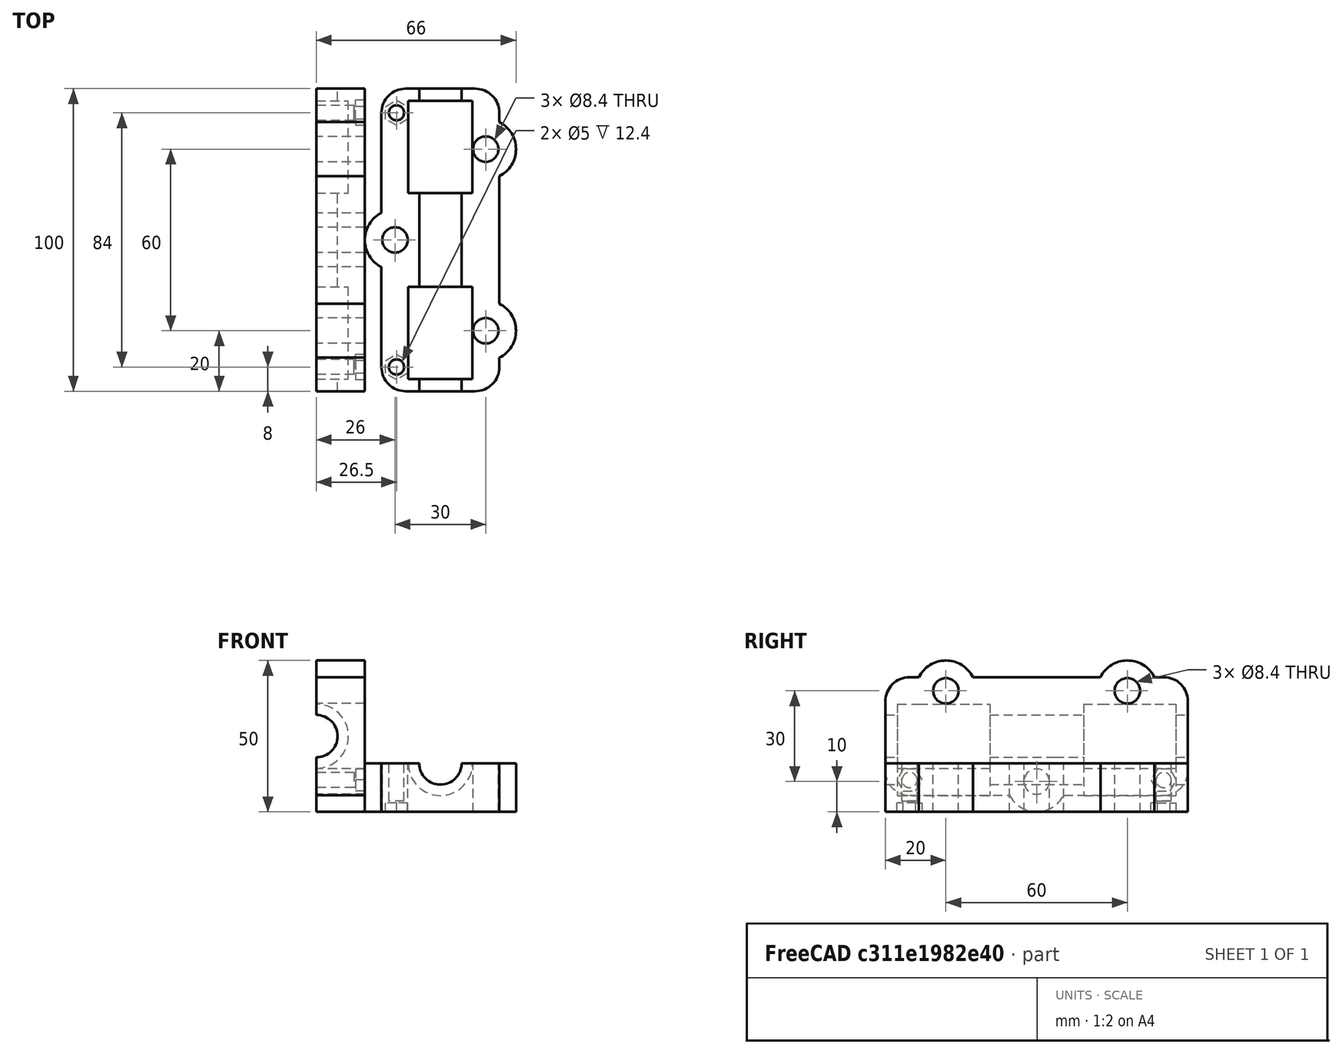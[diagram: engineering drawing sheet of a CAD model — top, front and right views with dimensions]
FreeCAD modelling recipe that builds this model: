
FCSTD DOCUMENT  (FreeCAD 0.15R4666 (Git))
Label: y_carriage_A
License: All rights reserved
LicenseURL: http://en.wikipedia.org/wiki/All_rights_reserved
objects: Part::Cylinder×11, Part::MultiFuse×5, Part::Cut×5, Part::Feature×2, Part::Prism×2, Mesh::Feature×1, Part::Box×1, Part::Fillet×1
note: 27 computed .brp shape members not serialized (recipe doc carries the construction recipe); baked Part::Feature solids carry a one-line shape summary decoded from their .brp

FEATURE [Mesh::Feature] Ycariage2_12mm
FEATURE [Part::Feature] Ycariage2_12mm001001  label="Ycariage2_12mm002"
  shape: bbox 50 x 100 x 16 mm, 1404 faces, 0 solids (baked)
FEATURE [Part::Box] Box  label="Cubo"
  Height = 16
  Length = 39
  Placement = pos=(5.5,0,0) rot=(0,0,1;0rad)
  Width = 100
FEATURE [Part::Cylinder] Cylinder  label="Cilindro"
  Angle = 360
  Height = 16
  Placement = pos=(40,20,0) rot=(0,0,1;0rad)
  Radius = 10
FEATURE [Part::Cylinder] Cylinder001  label="Cilindro001"
  Angle = 360
  Height = 16
  Placement = pos=(10,50,0) rot=(0,0,1;0rad)
  Radius = 10
FEATURE [Part::Cylinder] Cylinder002  label="Cilindro002"
  Angle = 360
  Height = 16
  Placement = pos=(40,80,0) rot=(0,0,1;0rad)
  Radius = 10
FEATURE [Part::Prism] Prism  label="Prisma"
  Circumradius = 4.2
  Height = 4
  Placement = pos=(10.5,8,-1) rot=(0,0,1;0.523599rad)
  Polygon = 6
FEATURE [Part::Prism] Prism001  label="Prisma001"
  Circumradius = 4.2
  Height = 4
  Placement = pos=(10.5,92,-1) rot=(0,0,1;0.523599rad)
  Polygon = 6
FEATURE [Part::MultiFuse] Fusion  label="body_base"
  Shapes = -> [Cylinder001,Cylinder,Cylinder002,Box]
FEATURE [Part::Fillet] Fillet
  Base = -> Fusion
  Edges = 4 edges r=8: [Edge2,Edge4,Edge28,Edge30]
FEATURE [Part::MultiFuse] Fusion001  label="nuts_space"
  Shapes = -> [Prism001,Prism]
FEATURE [Part::Cut] Cut  label="body"
  Base = -> Fillet
  Tool = -> Fusion001
FEATURE [Part::Cylinder] Cylinder003  label="threaded_rod_hole_1"
  Angle = 360
  Height = 18
  Placement = pos=(10,50,-1) rot=(0,0,1;0rad)
  Radius = 4.2
FEATURE [Part::Cylinder] Cylinder004  label="threaded_rod_hole_2"
  Angle = 360
  Height = 18
  Placement = pos=(40,80,-1) rot=(0,0,1;0rad)
  Radius = 4.2
FEATURE [Part::Cylinder] Cylinder005  label="threaded_rod_hole_3"
  Angle = 360
  Height = 18
  Placement = pos=(40,20,-1) rot=(0,0,1;0rad)
  Radius = 4.2
FEATURE [Part::MultiFuse] Fusion002  label="threaded_rod_holes"
  Shapes = -> [Cylinder003,Cylinder004,Cylinder005]
FEATURE [Part::Cut] Cut001  label="body_with_tr_holes"
  Base = -> Cut
  Tool = -> Fusion002
FEATURE [Part::Cylinder] Cylinder006  label="screw_hole_1"
  Angle = 360
  Height = 13
  Placement = pos=(10.5,8,3.6) rot=(0,0,1;0rad)
  Radius = 2.5
FEATURE [Part::Cylinder] Cylinder007  label="screw_hole_2"
  Angle = 360
  Height = 13
  Placement = pos=(10.5,92,3.6) rot=(0,0,1;0rad)
  Radius = 2.5
FEATURE [Part::MultiFuse] Fusion003  label="screw_holes"
  Shapes = -> [Cylinder006,Cylinder007]
FEATURE [Part::Cut] Cut002  label="body_with_sc_and_ tr_holes"
  Base = -> Cut001
  Tool = -> Fusion003
FEATURE [Part::Cylinder] Cylinder008  label="y_threaded_rod_hole"
  Angle = 360
  Height = 102
  Placement = pos=(25,-1,16) rot=(-1,0,0;1.5708rad)
  Radius = 7
FEATURE [Part::Cut] Cut003  label="body_sr_trs_holes"
  Base = -> Cut002
  Tool = -> Cylinder008
FEATURE [Part::Cylinder] Cylinder009  label="bearing_1"
  Angle = 360
  Height = 30.5
  Placement = pos=(25,4,16) rot=(-1,0,0;1.5708rad)
  Radius = 10.6
FEATURE [Part::Cylinder] Cylinder010  label="bearing_2"
  Angle = 360
  Height = 30.5
  Placement = pos=(25,65.5,16) rot=(-1,0,0;1.5708rad)
  Radius = 10.6
FEATURE [Part::MultiFuse] Fusion004  label="bearings_holes"
  Shapes = -> [Cylinder009,Cylinder010]
FEATURE [Part::Cut] Cut004  label="y_carriage_A"
  Base = -> Cut003
  Tool = -> Fusion004
FEATURE [Part::Feature] Cut004_solid  label="y_carriage_A (Solid)"
  Placement = pos=(0,0,0) rot=(0,-1,0;1.5708rad)
  shape: bbox 16 x 100 x 50 mm, 47 faces (baked)
